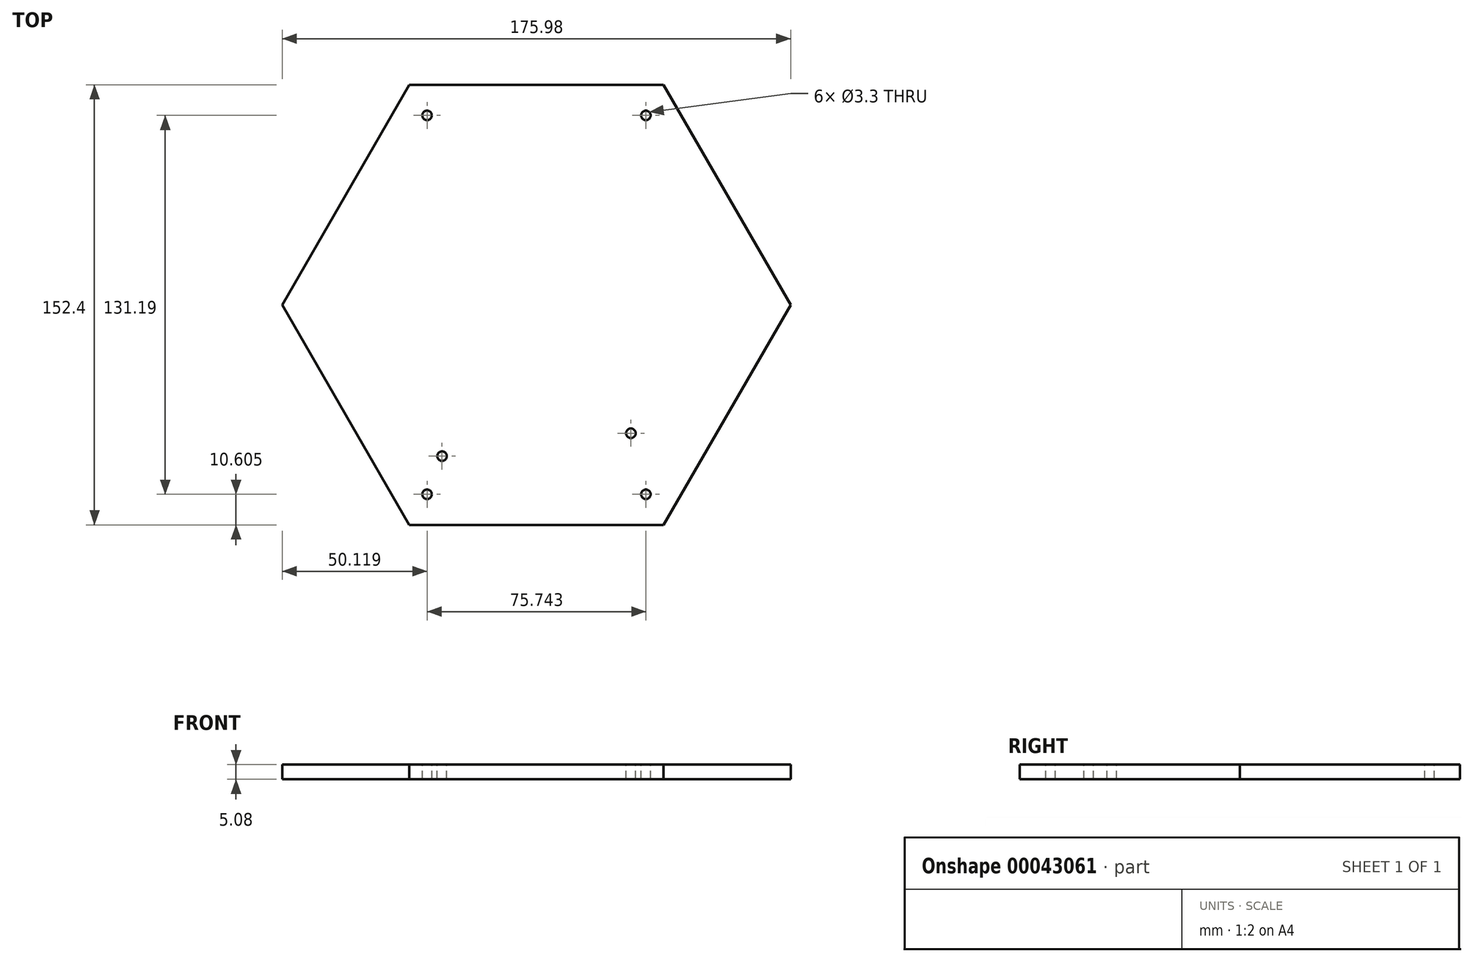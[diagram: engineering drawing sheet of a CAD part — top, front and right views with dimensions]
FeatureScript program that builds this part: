
annotation { "Feature Type Name" : "Feature", "Feature Type Description" : "" }
export const myFeature = defineFeature(function(context is Context, id is Id, definition is map)
    precondition{}
    {
        {
            var Q0;
            Q0=qCreatedBy(makeId("Top.planeOp"),FACE);
            var sketch = newSketch(context, id + "F0", { "sketchPlane" : qUnion([Q0])});
            skCircle(sketch, "E0.cCircle", {"center": v(0, 0) * mm, "radius": 76.2 * mm, "construction": true});
            skLineSegment(sketch, "E0.0", {"start": v(-44, 76.2) * mm, "end": v(44, 76.2) * mm});
            skLineSegment(sketch, "E0.1", {"start": v(44, 76.2) * mm, "end": v(87.99, 0) * mm});
            skLineSegment(sketch, "E0.2", {"start": v(87.99, 0) * mm, "end": v(44, -76.2) * mm});
            skLineSegment(sketch, "E0.3", {"start": v(44, -76.2) * mm, "end": v(-44, -76.2) * mm});
            skLineSegment(sketch, "E0.4", {"start": v(-44, -76.2) * mm, "end": v(-87.99, 0) * mm});
            skLineSegment(sketch, "E0.5", {"start": v(-87.99, 0) * mm, "end": v(-44, 76.2) * mm});
            skPoint(sketch, "E0.0.midPoint", {"position": v(0, 76.2) * mm});
            skSolve(sketch);
        }
        {
            var Q0;
            Q0=makeQuery(id+"F0.imprint","IMPRINT",FACE,{"disambiguationData":[TD([[makeQuery(id+"F0.imprint","IMPRINT",EDGE,{"derivedFrom":sQuery(id+"F0.wireOp",EDGE,"E0.0")}),-1.0]])]});
            extrude(context, id + "F1", {"entities" : qUnion([Q0]), "depth" : 5.08 * mm});
        }
        {
            var Q0;
            Q0=makeQuery(id+"F1.opExtrude","CAP_FACE",FACE,{"disambiguationData":[OSD([sQuery(id+"F0.wireOp",EDGE,"E0.0"),sQuery(id+"F0.wireOp",EDGE,"E0.1"),sQuery(id+"F0.wireOp",EDGE,"E0.2"),sQuery(id+"F0.wireOp",EDGE,"E0.3"),sQuery(id+"F0.wireOp",EDGE,"E0.4"),sQuery(id+"F0.wireOp",EDGE,"E0.5")])],"isStart":false});
            var sketch = newSketch(context, id + "F2", { "sketchPlane" : qUnion([Q0])});
            skLineSegment(sketch, "E1", {"start": v(-44, 76.2) * mm, "end": v(-37.87, 65.6) * mm});
            skLineSegment(sketch, "E2", {"start": v(44, 76.2) * mm, "end": v(37.87, 65.6) * mm});
            skLineSegment(sketch, "E3", {"start": v(44, -76.2) * mm, "end": v(37.87, -65.6) * mm});
            skLineSegment(sketch, "E4", {"start": v(-44, -76.2) * mm, "end": v(-37.87, -65.6) * mm});
            skCircle(sketch, "E5", {"center": v(-37.87, 65.6) * mm, "radius": 1.65 * mm});
            skCircle(sketch, "E6", {"center": v(37.87, 65.6) * mm, "radius": 1.65 * mm});
            skCircle(sketch, "E7", {"center": v(37.87, -65.6) * mm, "radius": 1.65 * mm});
            skCircle(sketch, "E8", {"center": v(-37.87, -65.6) * mm, "radius": 1.65 * mm});
            skSolve(sketch);
        }
        {
            var Q0;
            Q0 = qSketchRegion(id + "F2", true);
            extrude(context, id + "F3", {"entities" : qUnion([Q0]), "operationType" : NewBodyOperationType.REMOVE, "oppositeDirection" : true, "depth" : 25.4 * mm});
        }
        {
            var Q0;
            Q0=makeQuery(id+"F1.opExtrude","CAP_FACE",FACE,{"disambiguationData":[OSD([sQuery(id+"F0.wireOp",EDGE,"E0.0"),sQuery(id+"F0.wireOp",EDGE,"E0.1"),sQuery(id+"F0.wireOp",EDGE,"E0.2"),sQuery(id+"F0.wireOp",EDGE,"E0.3"),sQuery(id+"F0.wireOp",EDGE,"E0.4"),sQuery(id+"F0.wireOp",EDGE,"E0.5")])],"isStart":false});
            var sketch = newSketch(context, id + "F4", { "sketchPlane" : qUnion([Q0])});
            skLineSegment(sketch, "E9", {"start": v(32.69, -76.2) * mm, "end": v(32.69, -44.45) * mm});
            skCircle(sketch, "E10", {"center": v(32.69, -44.45) * mm, "radius": 1.65 * mm});
            skSolve(sketch);
        }
        {
            var Q0;
            Q0 = qSketchRegion(id + "F4", true);
            extrude(context, id + "F5", {"entities" : qUnion([Q0]), "operationType" : NewBodyOperationType.REMOVE, "oppositeDirection" : true, "depth" : 25.4 * mm});
        }
        {
            var Q0;
            Q0=makeQuery(id+"F1.opExtrude","CAP_FACE",FACE,{"disambiguationData":[OSD([sQuery(id+"F0.wireOp",EDGE,"E0.0"),sQuery(id+"F0.wireOp",EDGE,"E0.1"),sQuery(id+"F0.wireOp",EDGE,"E0.2"),sQuery(id+"F0.wireOp",EDGE,"E0.3"),sQuery(id+"F0.wireOp",EDGE,"E0.4"),sQuery(id+"F0.wireOp",EDGE,"E0.5")])],"isStart":false});
            var sketch = newSketch(context, id + "F6", { "sketchPlane" : qUnion([Q0])});
            skLineSegment(sketch, "E11", {"start": v(-32.69, -76.2) * mm, "end": v(-32.69, -52.39) * mm});
            skCircle(sketch, "E12", {"center": v(-32.69, -52.39) * mm, "radius": 1.65 * mm});
            skSolve(sketch);
        }
        {
            var Q0;
            Q0=makeQuery(id+"F6.imprint","IMPRINT",FACE,{"disambiguationData":[TD([[makeQuery(id+"F6.imprint","IMPRINT",EDGE,{"derivedFrom":sQuery(id+"F6.wireOp",EDGE,"E12")}),1.0]])]});
            extrude(context, id + "F7", {"entities" : qUnion([Q0]), "operationType" : NewBodyOperationType.REMOVE, "oppositeDirection" : true, "depth" : 25.4 * mm});
        }
    });
